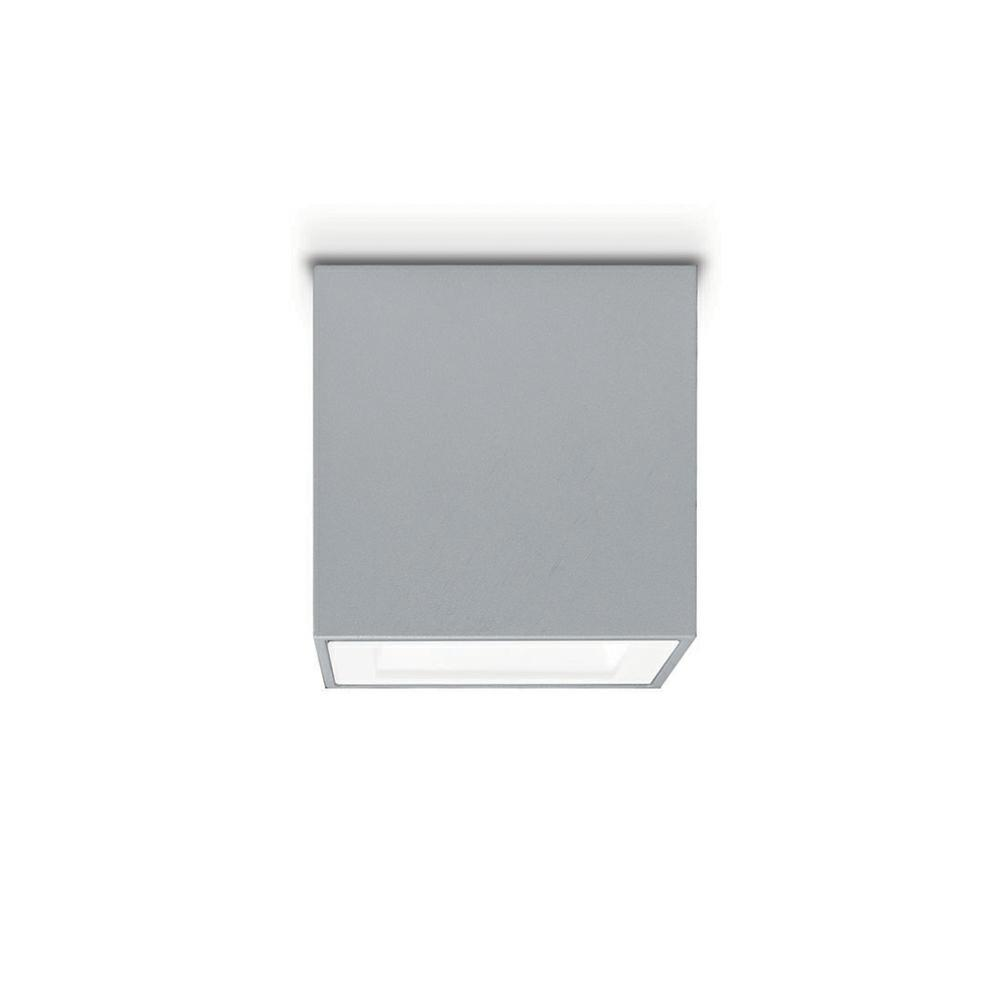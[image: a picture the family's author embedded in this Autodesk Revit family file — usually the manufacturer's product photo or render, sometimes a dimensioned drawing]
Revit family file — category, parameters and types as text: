
# Revit family: Platek_Mini One_Downlight
name_source: partatom
category: Apparecchi per illuminazione
revit_build: Autodesk Revit 2017 (Build: 20160225_1515(x64)
units: mm (PartAtom-declared; Revit-internal decimal feet)

## family parameters
Basato su piano di lavoro = No
Condiviso = No
Punto di calcolo locali = No
Quota connettore circolare = Usa diametro
Sempre verticale = Sì
Sorgente d'illuminazione = Sì
Taglio con vuoti quando caricato = No
Tipo di parte = Normale

## types (1)
- 1011615_7.8W_LED_3000K_Sanblasted glass
    Angolo inclinazione = 90.00°
    Beam Angle = 80.00°
    Body = PLK_06_Grey
    CRI = >80
    Cable Lenght = Cable input Ø 1÷13 mm
    Carico apparente = 0 VA
    Codice assieme = 1011615.06(Grey); 1011615.01(Black); 1011615.08(Anthracite); 1011615.07(Corten); 1011615.09(Bronze);
    Colour Temperature = 3000 K
    Commenti sul tipo = Suitable for restaurants, balconies, terraces
    Descrizione = Outdoor lighting, downlight, ceiling mounted
    Diffuse Type = Glass
    Dimmable = No
    Emetti da larghezza rettangolo = 85 mm  [stored 0.278871 ft]
    Emetti da lunghezza rettangolo = 85 mm  [stored 0.278871 ft]
    Energy Efficiency Rating = A/A+/A++
    File diagramma fotometrico = 1011615.IES
    Filtro dei colori = 16777215
    Frequency = 0/50/60 Hz
    IK Rating = IK 07
    IP Rating = IP65
    Immagine tipo = mini_one_1011615.jpg
    Insulation Class = 1
    LED Protection = Surge protection included
    Lampada = LED
    Light Source = PLK_Light Source
    Luminaire Luminous Flux = 433 lm
    Luminaire Luminous Intensity = 239 cd
    Luminaire Wattage = 8 W
    Manufacturer Comment = 5mm flat tempreted glass
    Modello = Mini One
    Mounting Type = Ceiling
    Nota chiave = Other Led colors available on request
    PLATEK Article Code = 1011615
    Power Supply Unit = Included
    Product Dimension = L100mm x L100mm x H100mm
    Product Documentation Link = http://www.platek.eu
    Product Page URL = http://www.platek.eu
    Produttore = PLATEK SRL
    Rendi la forma visibile nel rendering = No
    Supply Voltage = 230 V
    Supply Voltage Max = 240 V
    Supply Voltage Min = 220 V
    URL = www.platek.eu
    Variazione temperatura colore lampada con luminosità attenuata = <Nessuno>

note: [stored X ft] marks values corroborated as IEEE doubles in the binary element streams (Revit-internal decimal feet)
